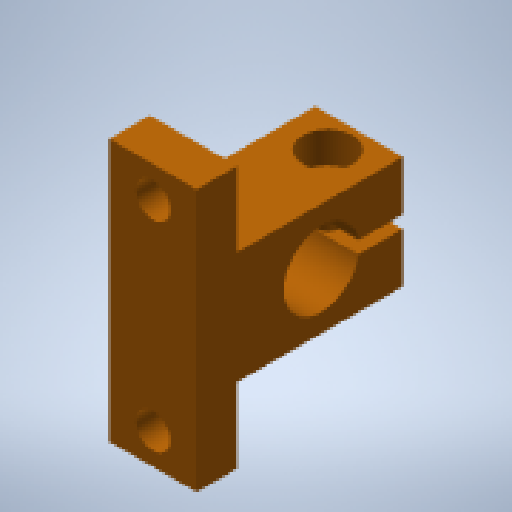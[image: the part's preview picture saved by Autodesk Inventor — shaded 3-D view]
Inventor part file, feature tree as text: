
AUTODESK INVENTOR PART (.ipt)
format: ipt  version: 2023 (Build 270158000, 158)  size: 280,576 bytes
history: native  units: mm
features: extrude x1, sketch x1
ambient origin geometry x8: Origin, YZ Plane, XZ Plane, XY Plane, X Axis, Y Axis, Z Axis, Center Point
bodies: Solid2 (feature_tree), Solid1 (feature_tree)
feature tree (2):
  extrude  "Extrusion1"  Depth=20.0mm TaperAngle=0.0deg
  sketch  "Sketch1"  dims[d0=12.0mm d1=20.0mm d2=0.0mm]
